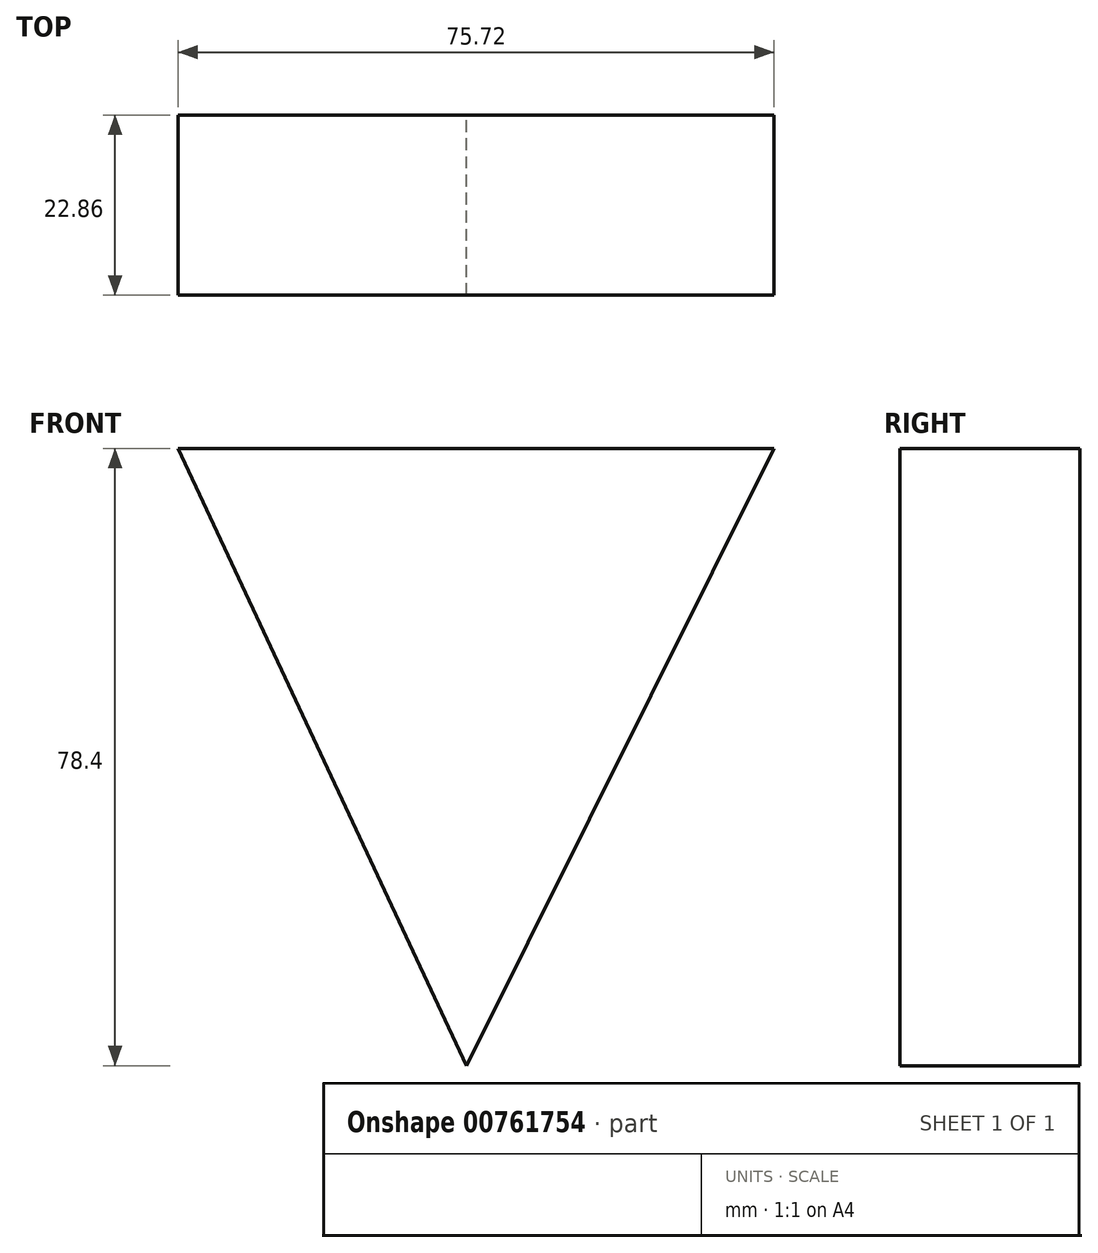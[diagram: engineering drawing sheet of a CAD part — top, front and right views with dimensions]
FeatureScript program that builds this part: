
annotation { "Feature Type Name" : "Feature", "Feature Type Description" : "" }
export const myFeature = defineFeature(function(context is Context, id is Id, definition is map)
    precondition{}
    {
        {
            var Q0;
            Q0=qCreatedBy(makeId("Front.planeOp"),FACE);
            var sketch = newSketch(context, id + "F0", { "sketchPlane" : qUnion([Q0])});
            skLineSegment(sketch, "E0", {"start": v(-36.65, 55.98) * mm, "end": v(39.07, 55.98) * mm});
            skLineSegment(sketch, "E1", {"start": v(39.07, 55.98) * mm, "end": v(0, -22.42) * mm});
            skLineSegment(sketch, "E2", {"start": v(0, -22.42) * mm, "end": v(-36.65, 55.98) * mm});
            skSolve(sketch);
        }
        {
            var Q0;
            Q0=makeQuery(id+"F0.imprint","IMPRINT",FACE,{"disambiguationData":[TD([[makeQuery(id+"F0.imprint","IMPRINT",EDGE,{"derivedFrom":sQuery(id+"F0.wireOp",EDGE,"E0")}),-1.0]])]});
            extrude(context, id + "F1", {"entities" : qUnion([Q0]), "depth" : 22.86 * mm, "offsetDistance" : 25.4 * mm});
        }
    });
